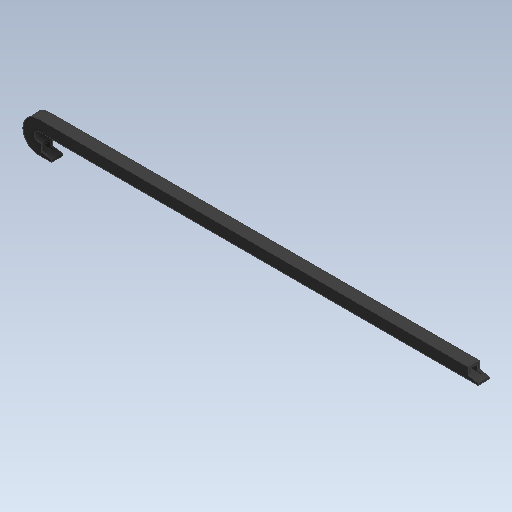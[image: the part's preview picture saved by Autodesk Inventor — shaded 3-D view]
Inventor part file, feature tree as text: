
AUTODESK INVENTOR PART (.ipt)
format: ipt  version: 2020 (Build 240168000, 168)  size: 140,288 bytes
history: native  units: mm
features: sketch x3, plane x1, sweep x1, extrude x1
ambient origin geometry x8: Origin, YZ Plane, XZ Plane, XY Plane, X Axis, Y Axis, Z Axis, Center Point
bodies: Solid1 (feature_tree)
feature tree (6):
  sketch  "Sketch1"  dims[d0=438.0mm d1=20.0mm]
  plane  "Work Plane1"
  sweep  "Sweep1"
  extrude  "Extrusion1"  Depth=7.0mm
  sketch  "Sketch2"  dims[d2=7.0mm d3=7.0mm]
  sketch  "Sketch3"  dims[d4=2.0mm d5=0.0mm d6=0.0mm d7=10.0mm d9=17.453293mm d10=2.0mm d11=0.0mm d12=0.0mm d13=10.0mm d18=17.453293mm d19=2.0mm]
